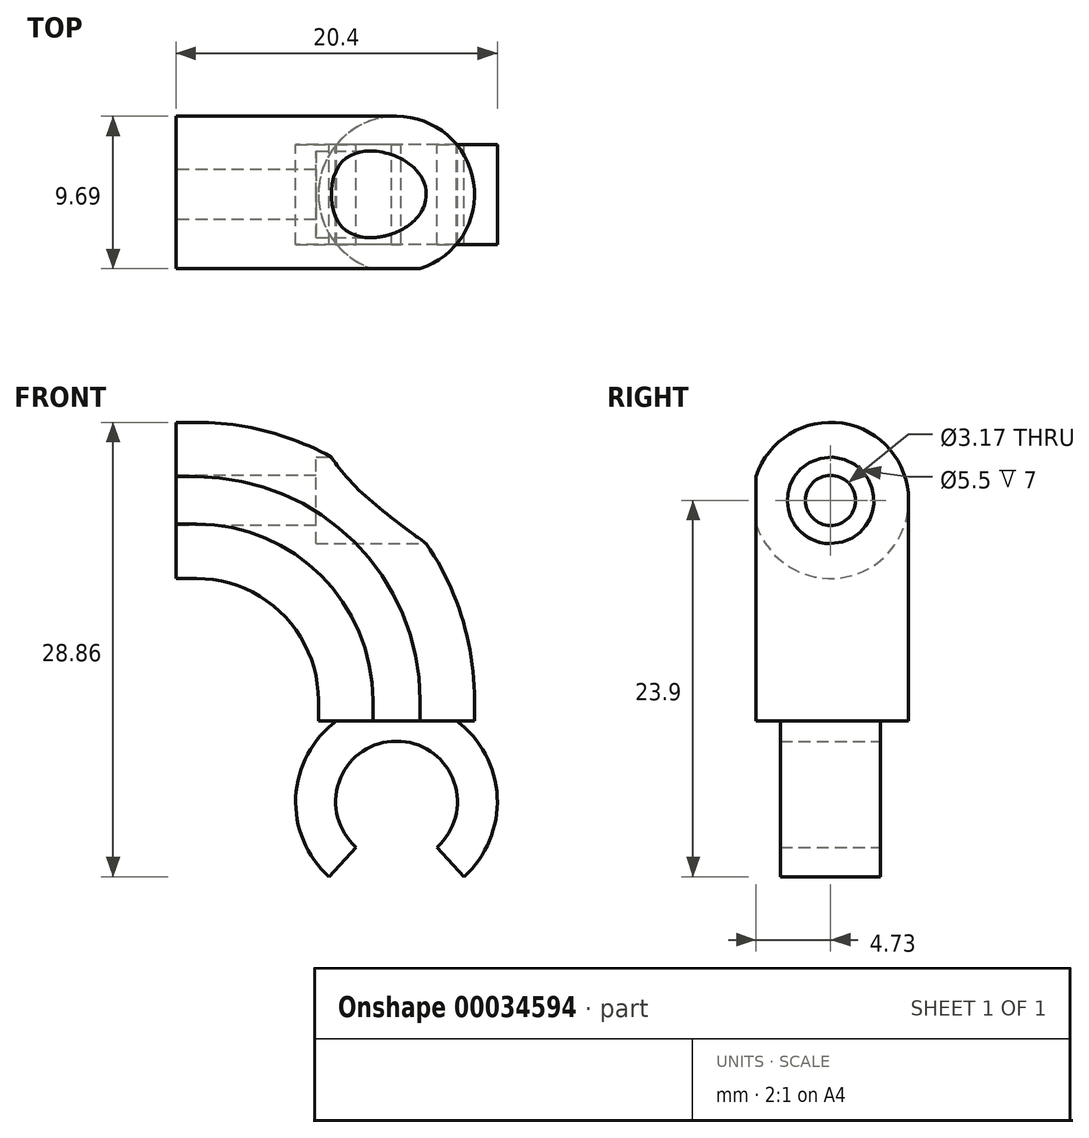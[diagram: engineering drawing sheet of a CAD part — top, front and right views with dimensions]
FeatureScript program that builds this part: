
annotation { "Feature Type Name" : "Feature", "Feature Type Description" : "" }
export const myFeature = defineFeature(function(context is Context, id is Id, definition is map)
    precondition{}
    {
        {
            var Q0;
            Q0=qCreatedBy(makeId("Front.planeOp"),FACE);
            var sketch = newSketch(context, id + "F0", { "sketchPlane" : qUnion([Q0])});
            skLineSegment(sketch, "E0", {"start": v(0, 0) * mm, "end": v(1.3, 0) * mm});
            skLineSegment(sketch, "E1", {"start": v(14, -12.7) * mm, "end": v(14, -14) * mm});
            skPoint(sketch, "E2.visualSharp", {"position": v(14, 0) * mm});
            skArc(sketch, "E2.filletArc", {"start": v(14, -12.7) * mm, "mid": v(10.28, -3.72) * mm, "end": v(1.3, 0) * mm});
            skSolve(sketch);
        }
        {
            var Q0;
            Q0=qCreatedBy(makeId("Right.planeOp"),FACE);
            var sketch = newSketch(context, id + "F1", { "sketchPlane" : qUnion([Q0])});
            skCircle(sketch, "E3", {"center": v(0, 0) * mm, "radius": 4.96 * mm});
            skSolve(sketch);
        }
        {
            var Q0;
            Q0=makeQuery(id+"F1.imprint","IMPRINT",FACE,{"disambiguationData":[TD([[makeQuery(id+"F1.imprint","IMPRINT",EDGE,{"derivedFrom":sQuery(id+"F1.wireOp",EDGE,"E3")}),1.0]])]});
            var Q1;
            Q1=sQuery(id+"F0.wireOp",EDGE,"E0");
            var Q2;
            Q2=sQuery(id+"F0.wireOp",EDGE,"E2.filletArc");
            var Q3;
            Q3=sQuery(id+"F0.wireOp",EDGE,"E1");
            sweep(context, id + "F2", {"profiles" : qUnion([Q0]), "path" : qUnion([Q1, Q2, Q3])});
        }
        {
            var Q0;
            Q0=makeQuery(id+"F2.opSweep","CAP_FACE",FACE,{"disambiguationData":[OSD([sQuery(id+"F0.wireOp",VERTEX,"E0.start"),sQuery(id+"F1.wireOp",EDGE,"E3")])],"isStart":true});
            var sketch = newSketch(context, id + "F3", { "sketchPlane" : qUnion([Q0])});
            skCircle(sketch, "E4", {"center": v(0, 0) * mm, "radius": 1.59 * mm});
            skSolve(sketch);
        }
        {
            var Q0;
            Q0=qSketchRegion(id+"F3",true);
            extrude(context, id + "F4", {"entities" : qUnion([Q0]), "operationType" : NewBodyOperationType.REMOVE, "endBound" : BoundingType.THROUGH_ALL, "oppositeDirection" : true, "depth" : 25.4 * mm});
        }
        {
            var Q0;
            Q0=qCreatedBy(makeId("Right.planeOp"),FACE);
            cPlane(context, id + "F5", {"entities" : qUnion([Q0]), "cplaneType" : CPlaneType.OFFSET, "offset" : 19.05 * mm, "width" : 152.4 * mm, "height" : 152.4 * mm});
        }
        {
            var Q0;
            Q0=qCreatedBy(id+"F5.planeOp",FACE);
            var sketch = newSketch(context, id + "F6", { "sketchPlane" : qUnion([Q0])});
            skCircle(sketch, "E5", {"center": v(0, 0) * mm, "radius": 2.75 * mm});
            skSolve(sketch);
        }
        {
            var Q0;
            Q0=qSketchRegion(id+"F6",true);
            extrude(context, id + "F7", {"entities" : qUnion([Q0]), "operationType" : NewBodyOperationType.REMOVE, "oppositeDirection" : true, "depth" : 10.16 * mm});
        }
        {
            var Q0;
            Q0=qCreatedBy(makeId("Front.planeOp"),FACE);
            var sketch = newSketch(context, id + "F8", { "sketchPlane" : qUnion([Q0])});
            skLineSegment(sketch, "E6", {"start": v(14, -14) * mm, "end": v(14, -19.15) * mm, "construction": true});
            skLineSegment(sketch, "E7", {"start": v(14, -14) * mm, "end": v(10.19, -14) * mm});
            skArc(sketch, "E8", {"start": v(10.2, -14) * mm, "mid": v(7.6, -18.84) * mm, "end": v(9.71, -23.9) * mm});
            skArc(sketch, "E9.0", {"start": v(13.7, -15.3) * mm, "mid": v(10.34, -17.9) * mm, "end": v(11.42, -22.03) * mm});
            skLineSegment(sketch, "E10", {"start": v(13.7, -15.3) * mm, "end": v(14, -15.3) * mm});
            skLineSegment(sketch, "E11", {"start": v(11.42, -22.03) * mm, "end": v(9.71, -23.9) * mm});
            skLineSegment(sketch, "E12.MirrorCS", {"start": v(14.3, -15.3) * mm, "end": v(14, -15.3) * mm});
            skLineSegment(sketch, "E13.MirrorCS", {"start": v(14, -14) * mm, "end": v(17.8, -14) * mm});
            skArc(sketch, "E14.MirrorCS", {"start": v(17.8, -14) * mm, "mid": v(20.4, -18.84) * mm, "end": v(18.29, -23.9) * mm});
            skArc(sketch, "E15.MirrorCS", {"start": v(14.3, -15.3) * mm, "mid": v(17.66, -17.9) * mm, "end": v(16.58, -22.03) * mm});
            skLineSegment(sketch, "E16.MirrorCS", {"start": v(16.58, -22.03) * mm, "end": v(18.29, -23.9) * mm});
            skSolve(sketch);
        }
        {
            var Q0;
            Q0=qSketchRegion(id+"F8",true);
            extrude(context, id + "F9", {"entities" : qUnion([Q0]), "operationType" : NewBodyOperationType.ADD, "endBound" : BoundingType.SYMMETRIC, "depth" : 6.35 * mm});
        }
        {
            var Q0;
            Q0=qCreatedBy(makeId("Right.planeOp"),FACE);
            var sketch = newSketch(context, id + "F10", { "sketchPlane" : qUnion([Q0])});
            skLineSegment(sketch, "E17", {"start": v(0, 0) * mm, "end": v(0, -19.18) * mm, "construction": true});
            skLineSegment(sketch, "E18.MirrorCS", {"start": v(-4.73, -14) * mm, "end": v(-4.73, 5.05) * mm});
            skLineSegment(sketch, "E19.MirrorCS", {"start": v(-4.98, -14) * mm, "end": v(-4.98, 5.05) * mm});
            skLineSegment(sketch, "E20", {"start": v(-4.98, 5.05) * mm, "end": v(-4.73, 5.05) * mm});
            skLineSegment(sketch, "E21", {"start": v(-4.73, -14) * mm, "end": v(-4.98, -14) * mm});
            skSolve(sketch);
        }
        {
            var Q0;
            Q0=qSketchRegion(id+"F10",true);
            extrude(context, id + "F11", {"entities" : qUnion([Q0]), "operationType" : NewBodyOperationType.REMOVE, "endBound" : BoundingType.THROUGH_ALL, "depth" : 25.4 * mm});
        }
    });
